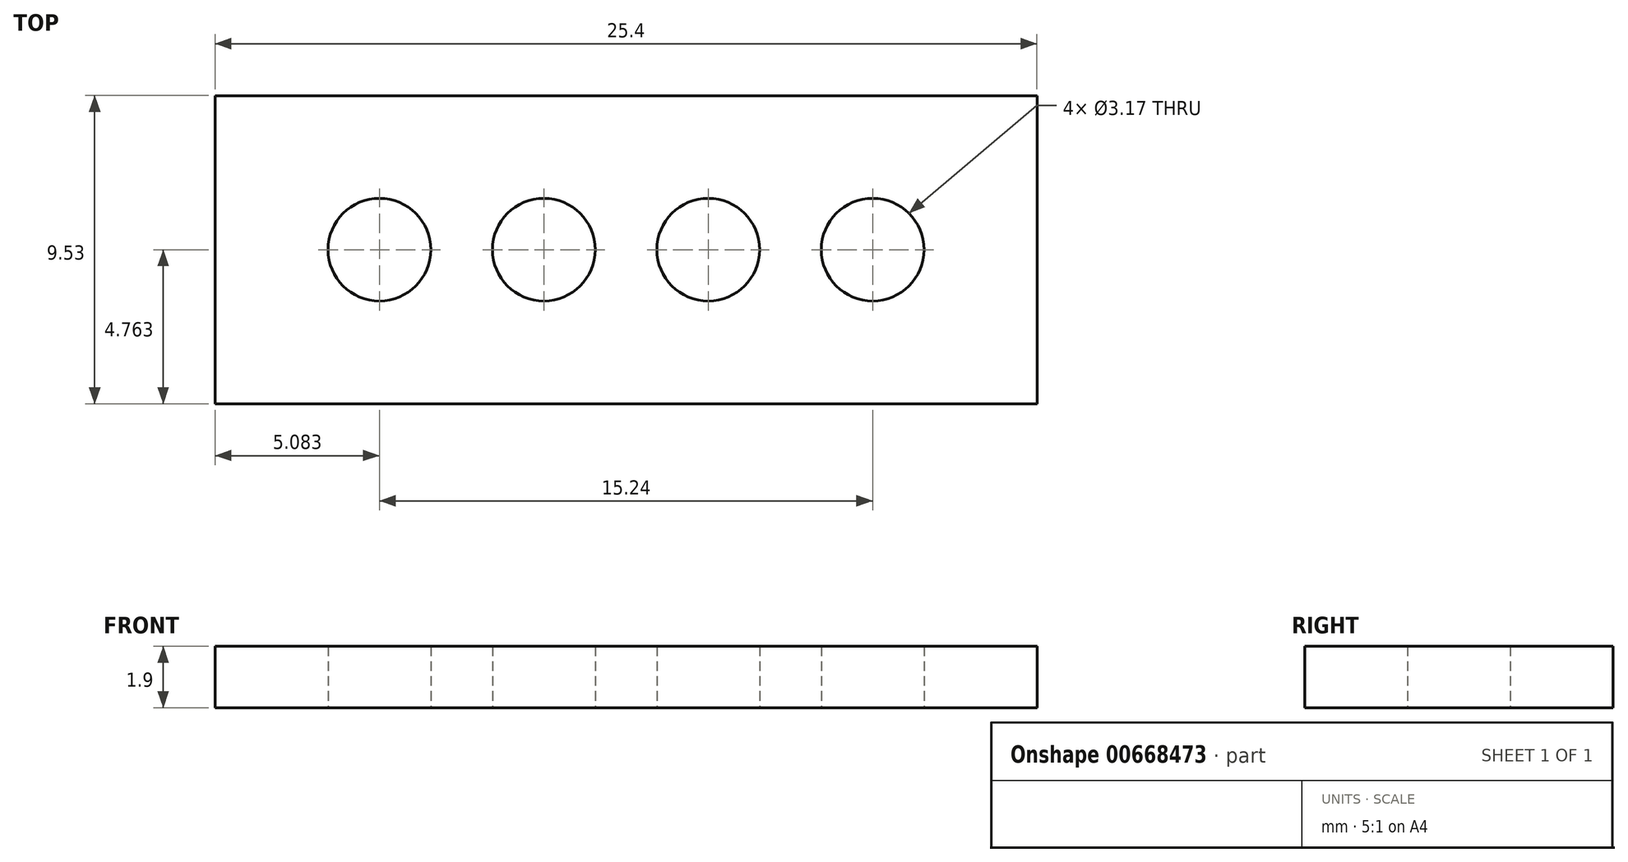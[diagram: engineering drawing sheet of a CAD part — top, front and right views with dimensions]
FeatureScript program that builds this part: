
annotation { "Feature Type Name" : "Feature", "Feature Type Description" : "" }
export const myFeature = defineFeature(function(context is Context, id is Id, definition is map)
    precondition{}
    {
        {
            var Q0;
            Q0=qCreatedBy(makeId("Top.planeOp"),FACE);
            var sketch = newSketch(context, id + "F0", { "sketchPlane" : qUnion([Q0])});
            skLineSegment(sketch, "E0.bottom", {"start": v(-35.28, 21.73) * mm, "end": v(-9.88, 21.73) * mm});
            skLineSegment(sketch, "E0.top", {"start": v(-35.28, 12.2) * mm, "end": v(-9.88, 12.2) * mm});
            skLineSegment(sketch, "E0.left", {"start": v(-35.28, 21.73) * mm, "end": v(-35.28, 12.2) * mm});
            skLineSegment(sketch, "E0.right", {"start": v(-9.88, 21.73) * mm, "end": v(-9.88, 12.2) * mm});
            skCircle(sketch, "E1", {"center": v(-30.2, 16.96) * mm, "radius": 1.59 * mm});
            skCircle(sketch, "E2", {"center": v(-25.12, 16.96) * mm, "radius": 1.59 * mm});
            skCircle(sketch, "E3", {"center": v(-20.04, 16.96) * mm, "radius": 1.59 * mm});
            skCircle(sketch, "E4", {"center": v(-14.96, 16.96) * mm, "radius": 1.59 * mm});
            skPoint(sketch, "E5.orphan", {"position": v(-35.28, 16.96) * mm});
            skPoint(sketch, "E6.trimOffspring.end.orphan", {"position": v(-9.88, 16.96) * mm});
            skSolve(sketch);
        }
        {
            var Q0;
            Q0=makeQuery(id+"F0.imprint","IMPRINT",FACE,{"disambiguationData":[TD([[makeQuery(id+"F0.imprint","IMPRINT",EDGE,{"derivedFrom":sQuery(id+"F0.wireOp",EDGE,"E0.bottom")}),-1.0]])]});
            extrude(context, id + "F1", {"entities" : qUnion([Q0]), "depth" : 1.9 * mm});
        }
    });
